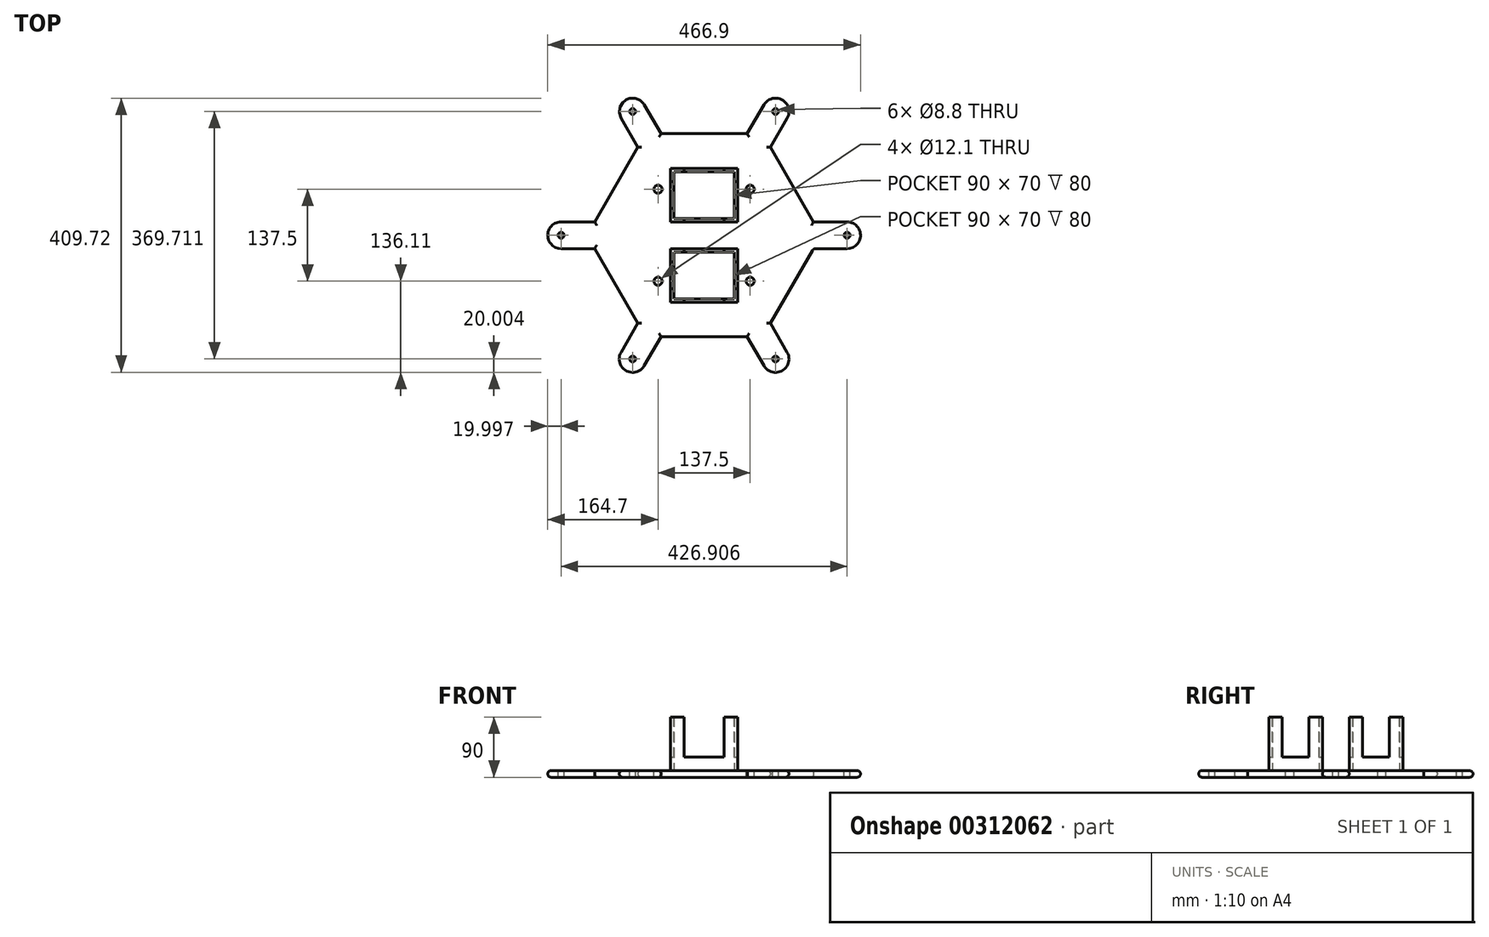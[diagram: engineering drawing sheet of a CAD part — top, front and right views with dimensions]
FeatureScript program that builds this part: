
annotation { "Feature Type Name" : "Feature", "Feature Type Description" : "" }
export const myFeature = defineFeature(function(context is Context, id is Id, definition is map)
    precondition{}
    {
        {
            var Q0;
            Q0=qCreatedBy(makeId("Top.planeOp"),FACE);
            var sketch = newSketch(context, id + "F0", { "sketchPlane" : qUnion([Q0])});
            skCircle(sketch, "E0.cCircle", {"center": v(0, 0) * mm, "radius": 175 * mm, "construction": true});
            skLineSegment(sketch, "E0.0", {"start": v(-87.5, 151.55) * mm, "end": v(87.5, 151.55) * mm});
            skLineSegment(sketch, "E0.1", {"start": v(87.5, 151.55) * mm, "end": v(175, 0) * mm});
            skLineSegment(sketch, "E0.2", {"start": v(175, 0) * mm, "end": v(87.5, -151.55) * mm});
            skLineSegment(sketch, "E0.3", {"start": v(87.5, -151.55) * mm, "end": v(-87.5, -151.55) * mm});
            skLineSegment(sketch, "E0.4", {"start": v(-87.5, -151.55) * mm, "end": v(-175, 0) * mm});
            skLineSegment(sketch, "E0.5", {"start": v(-175, 0) * mm, "end": v(-87.5, 151.55) * mm});
            skLineSegment(sketch, "E1.bottom", {"start": v(-213.45, 20) * mm, "end": v(-163.45, 20) * mm});
            skLineSegment(sketch, "E1.top", {"start": v(-213.45, -20) * mm, "end": v(-163.45, -20) * mm});
            skLineSegment(sketch, "E1.left", {"start": v(-213.45, 20) * mm, "end": v(-213.45, -20) * mm});
            skPoint(sketch, "E2.startSnap0", {"position": v(0, 151.55) * mm});
            skPoint(sketch, "E2.endSnap0", {"position": v(0, -151.55) * mm});
            skLineSegment(sketch, "E3", {"start": v(-175, 0) * mm, "end": v(-213.45, 0) * mm, "construction": true});
            skLineSegment(sketch, "E4.1.0", {"start": v(-124.05, -174.86) * mm, "end": v(-89.4, -194.86) * mm});
            skLineSegment(sketch, "E4.1.1", {"start": v(-124.05, -174.86) * mm, "end": v(-99.05, -131.55) * mm});
            skLineSegment(sketch, "E4.1.2", {"start": v(-89.4, -194.86) * mm, "end": v(-64.4, -151.55) * mm});
            skLineSegment(sketch, "E4.2.0", {"start": v(89.4, -194.86) * mm, "end": v(124.05, -174.86) * mm});
            skLineSegment(sketch, "E4.2.1", {"start": v(89.4, -194.86) * mm, "end": v(64.4, -151.55) * mm});
            skLineSegment(sketch, "E4.2.2", {"start": v(124.05, -174.86) * mm, "end": v(99.05, -131.55) * mm});
            skLineSegment(sketch, "E4.3.0", {"start": v(213.45, -20) * mm, "end": v(213.45, 20) * mm});
            skLineSegment(sketch, "E4.3.1", {"start": v(213.45, -20) * mm, "end": v(163.45, -20) * mm});
            skLineSegment(sketch, "E4.3.2", {"start": v(213.45, 20) * mm, "end": v(163.45, 20) * mm});
            skLineSegment(sketch, "E4.4.0", {"start": v(124.05, 174.86) * mm, "end": v(89.4, 194.86) * mm});
            skLineSegment(sketch, "E4.4.1", {"start": v(124.05, 174.86) * mm, "end": v(99.05, 131.55) * mm});
            skLineSegment(sketch, "E4.4.2", {"start": v(89.4, 194.86) * mm, "end": v(64.4, 151.55) * mm});
            skLineSegment(sketch, "E4.5.0", {"start": v(-89.4, 194.86) * mm, "end": v(-124.05, 174.86) * mm});
            skLineSegment(sketch, "E4.5.1", {"start": v(-89.4, 194.86) * mm, "end": v(-64.4, 151.55) * mm});
            skLineSegment(sketch, "E4.5.2", {"start": v(-124.05, 174.86) * mm, "end": v(-99.05, 131.55) * mm});
            skArc(sketch, "E5", {"start": v(-213.45, 20) * mm, "mid": v(-233.45, 0) * mm, "end": v(-213.45, -20) * mm});
            skArc(sketch, "E6.1.0", {"start": v(-124.05, -174.86) * mm, "mid": v(-116.73, -202.18) * mm, "end": v(-89.4, -194.86) * mm});
            skArc(sketch, "E6.2.0", {"start": v(89.4, -194.86) * mm, "mid": v(116.73, -202.18) * mm, "end": v(124.05, -174.86) * mm});
            skArc(sketch, "E6.3.0", {"start": v(213.45, -20) * mm, "mid": v(233.45, 0) * mm, "end": v(213.45, 20) * mm});
            skArc(sketch, "E6.4.0", {"start": v(124.05, 174.86) * mm, "mid": v(116.73, 202.18) * mm, "end": v(89.4, 194.86) * mm});
            skArc(sketch, "E6.5.0", {"start": v(-89.4, 194.86) * mm, "mid": v(-116.73, 202.18) * mm, "end": v(-124.05, 174.86) * mm});
            skSolve(sketch);
        }
        {
            var Q0;
            Q0=qSketchRegion(id+"F0",true);
            extrude(context, id + "F1", {"entities" : qUnion([Q0]), "depth" : 10 * mm});
        }
        {
            var Q0;
            Q0=makeQuery(id+"F1.opExtrude","CAP_FACE",FACE,{"disambiguationData":[OSD([sQuery(id+"F0.wireOp",EDGE,"E0.0"),sQuery(id+"F0.wireOp",EDGE,"E0.1"),sQuery(id+"F0.wireOp",EDGE,"E0.2"),sQuery(id+"F0.wireOp",EDGE,"E0.3"),sQuery(id+"F0.wireOp",EDGE,"E0.4"),sQuery(id+"F0.wireOp",EDGE,"E0.5"),sQuery(id+"F0.wireOp",EDGE,"E1.bottom"),sQuery(id+"F0.wireOp",EDGE,"E1.top"),sQuery(id+"F0.wireOp",EDGE,"E4.1.1"),sQuery(id+"F0.wireOp",EDGE,"E4.1.2"),sQuery(id+"F0.wireOp",EDGE,"E4.2.1"),sQuery(id+"F0.wireOp",EDGE,"E4.2.2"),sQuery(id+"F0.wireOp",EDGE,"E4.3.1"),sQuery(id+"F0.wireOp",EDGE,"E4.3.2"),sQuery(id+"F0.wireOp",EDGE,"E4.4.1"),sQuery(id+"F0.wireOp",EDGE,"E4.4.2"),sQuery(id+"F0.wireOp",EDGE,"E4.5.1"),sQuery(id+"F0.wireOp",EDGE,"E4.5.2"),sQuery(id+"F0.wireOp",EDGE,"E5"),sQuery(id+"F0.wireOp",EDGE,"E6.1.0"),sQuery(id+"F0.wireOp",EDGE,"E6.2.0"),sQuery(id+"F0.wireOp",EDGE,"E6.3.0"),sQuery(id+"F0.wireOp",EDGE,"E6.4.0"),sQuery(id+"F0.wireOp",EDGE,"E6.5.0")])],"isStart":false});
            var sketch = newSketch(context, id + "F2", { "sketchPlane" : qUnion([Q0])});
            skCircle(sketch, "E7", {"center": v(0, 0) * mm, "radius": 137.5 * mm});
            skCircle(sketch, "E8", {"center": v(0, 0) * mm, "radius": 75 * mm});
            skLineSegment(sketch, "E9", {"start": v(137.5, 0) * mm, "end": v(0, 137.5) * mm});
            skLineSegment(sketch, "E10", {"start": v(0, 137.5) * mm, "end": v(-137.5, 0) * mm});
            skLineSegment(sketch, "E11", {"start": v(-137.5, 0) * mm, "end": v(0, -137.5) * mm});
            skLineSegment(sketch, "E12", {"start": v(0, -137.5) * mm, "end": v(137.5, 0) * mm});
            skLineSegment(sketch, "E13", {"start": v(-75, 0) * mm, "end": v(-106.25, 31.25) * mm});
            skLineSegment(sketch, "E14", {"start": v(0, 75) * mm, "end": v(-31.25, 106.25) * mm});
            skLineSegment(sketch, "E15", {"start": v(0, 75) * mm, "end": v(31.25, 106.25) * mm});
            skLineSegment(sketch, "E16", {"start": v(-75, 0) * mm, "end": v(-106.25, -31.25) * mm});
            skLineSegment(sketch, "E17", {"start": v(0, -75) * mm, "end": v(-31.25, -106.25) * mm});
            skLineSegment(sketch, "E18", {"start": v(0, -75) * mm, "end": v(31.25, -106.25) * mm});
            skLineSegment(sketch, "E19", {"start": v(75, 0) * mm, "end": v(106.25, 31.25) * mm});
            skLineSegment(sketch, "E20", {"start": v(75, 0) * mm, "end": v(106.25, -31.25) * mm});
            skLineSegment(sketch, "E21", {"start": v(0, 75) * mm, "end": v(0, -75) * mm, "construction": true});
            skLineSegment(sketch, "E22", {"start": v(-75, 0) * mm, "end": v(75, 0) * mm, "construction": true});
            skLineSegment(sketch, "E23", {"start": v(-10, 74.33) * mm, "end": v(-10, -74.33) * mm});
            skLineSegment(sketch, "E24", {"start": v(10, 74.33) * mm, "end": v(10, -74.33) * mm});
            skLineSegment(sketch, "E25", {"start": v(-74.33, 10) * mm, "end": v(74.33, 10) * mm});
            skLineSegment(sketch, "E26", {"start": v(74.33, -10) * mm, "end": v(-74.33, -10) * mm});
            skLineSegment(sketch, "E27", {"start": v(-68.75, 68.75) * mm, "end": v(68.75, -68.75) * mm, "construction": true});
            skLineSegment(sketch, "E28", {"start": v(-68.75, -68.75) * mm, "end": v(68.75, 68.75) * mm, "construction": true});
            skPoint(sketch, "E29", {"position": v(-68.75, 68.75) * mm});
            skPoint(sketch, "E30", {"position": v(68.75, 68.75) * mm});
            skPoint(sketch, "E31", {"position": v(-68.75, -68.75) * mm});
            skPoint(sketch, "E32", {"position": v(68.75, -68.75) * mm});
            skSolve(sketch);
        }
        {
            var Q0;
            Q0=makeQuery(id+"F1.opExtrude","CAP_FACE",FACE,{"disambiguationData":[OSD([sQuery(id+"F0.wireOp",EDGE,"E0.0"),sQuery(id+"F0.wireOp",EDGE,"E0.1"),sQuery(id+"F0.wireOp",EDGE,"E0.2"),sQuery(id+"F0.wireOp",EDGE,"E0.3"),sQuery(id+"F0.wireOp",EDGE,"E0.4"),sQuery(id+"F0.wireOp",EDGE,"E0.5"),sQuery(id+"F0.wireOp",EDGE,"E1.bottom"),sQuery(id+"F0.wireOp",EDGE,"E1.top"),sQuery(id+"F0.wireOp",EDGE,"E4.1.1"),sQuery(id+"F0.wireOp",EDGE,"E4.1.2"),sQuery(id+"F0.wireOp",EDGE,"E4.2.1"),sQuery(id+"F0.wireOp",EDGE,"E4.2.2"),sQuery(id+"F0.wireOp",EDGE,"E4.3.1"),sQuery(id+"F0.wireOp",EDGE,"E4.3.2"),sQuery(id+"F0.wireOp",EDGE,"E4.4.1"),sQuery(id+"F0.wireOp",EDGE,"E4.4.2"),sQuery(id+"F0.wireOp",EDGE,"E4.5.1"),sQuery(id+"F0.wireOp",EDGE,"E4.5.2"),sQuery(id+"F0.wireOp",EDGE,"E5"),sQuery(id+"F0.wireOp",EDGE,"E6.1.0"),sQuery(id+"F0.wireOp",EDGE,"E6.2.0"),sQuery(id+"F0.wireOp",EDGE,"E6.3.0"),sQuery(id+"F0.wireOp",EDGE,"E6.4.0"),sQuery(id+"F0.wireOp",EDGE,"E6.5.0")])],"isStart":false});
            var sketch = newSketch(context, id + "F3", { "sketchPlane" : qUnion([Q0])});
            skPoint(sketch, "E33", {"position": v(-213.45, 0) * mm});
            skPoint(sketch, "E34.1.0", {"position": v(-106.73, -184.86) * mm});
            skPoint(sketch, "E34.2.0", {"position": v(106.73, -184.86) * mm});
            skPoint(sketch, "E34.3.0", {"position": v(213.45, 0) * mm});
            skPoint(sketch, "E34.4.0", {"position": v(106.73, 184.86) * mm});
            skPoint(sketch, "E34.5.0", {"position": v(-106.73, 184.86) * mm});
            skPoint(sketch, "E34.center", {"position": v(0, 0) * mm});
            skSolve(sketch);
        }
        {
            var Q0;
            Q0=sQuery(id+"F3.wireOp",VERTEX,"E33");
            var Q1;
            Q1=sQuery(id+"F3.wireOp",VERTEX,"E34.5.0");
            var Q2;
            Q2=sQuery(id+"F3.wireOp",VERTEX,"E34.4.0");
            var Q3;
            Q3=sQuery(id+"F3.wireOp",VERTEX,"E34.3.0");
            var Q4;
            Q4=sQuery(id+"F3.wireOp",VERTEX,"E34.2.0");
            var Q5;
            Q5=sQuery(id+"F3.wireOp",VERTEX,"E34.1.0");
            var Q6;
            Q6=makeQuery(id+"F1.opExtrude","SWEPT_BODY",BODY,{"disambiguationData":[OSD([sQuery(id+"F0.wireOp",EDGE,"E0.0"),sQuery(id+"F0.wireOp",EDGE,"E0.1"),sQuery(id+"F0.wireOp",EDGE,"E0.2"),sQuery(id+"F0.wireOp",EDGE,"E0.3"),sQuery(id+"F0.wireOp",EDGE,"E0.4"),sQuery(id+"F0.wireOp",EDGE,"E0.5"),sQuery(id+"F0.wireOp",EDGE,"E1.bottom"),sQuery(id+"F0.wireOp",EDGE,"E1.top"),sQuery(id+"F0.wireOp",EDGE,"E4.1.1"),sQuery(id+"F0.wireOp",EDGE,"E4.1.2"),sQuery(id+"F0.wireOp",EDGE,"E4.2.1"),sQuery(id+"F0.wireOp",EDGE,"E4.2.2"),sQuery(id+"F0.wireOp",EDGE,"E4.3.1"),sQuery(id+"F0.wireOp",EDGE,"E4.3.2"),sQuery(id+"F0.wireOp",EDGE,"E4.4.1"),sQuery(id+"F0.wireOp",EDGE,"E4.4.2"),sQuery(id+"F0.wireOp",EDGE,"E4.5.1"),sQuery(id+"F0.wireOp",EDGE,"E4.5.2"),sQuery(id+"F0.wireOp",EDGE,"E5"),sQuery(id+"F0.wireOp",EDGE,"E6.1.0"),sQuery(id+"F0.wireOp",EDGE,"E6.2.0"),sQuery(id+"F0.wireOp",EDGE,"E6.3.0"),sQuery(id+"F0.wireOp",EDGE,"E6.4.0"),sQuery(id+"F0.wireOp",EDGE,"E6.5.0")])]});
            hole(context, id + "F4", {"style" : HoleStyle.SIMPLE, "endStyle" : HoleEndStyle.THROUGH, "standardTappedOrClearance" : lookupTablePath({ "standard" : "ISO", "engagement" : "75%", "pitch" : "1.25 mm", "size" : "M10", "type" : "Tapped" }), "standardBlindInLast" : lookupTablePath({ "standard" : "ISO", "engagement" : "75%", "pitch" : "1.25 mm", "size" : "M10", "type" : "Tapped" }), "holeDiameter" : 8.8 * mm, "showTappedDepth" : true, "tappedDepth" : 6 * mm, "tapClearance" : 3, "locations" : qUnion([Q0, Q1, Q2, Q3, Q4, Q5]), "scope" : qUnion([Q6]), "majorDiameter" : 10 * mm});
        }
        {
            var Q0;
            Q0=sQuery(id+"F2.wireOp",VERTEX,"E29");
            var Q1;
            Q1=sQuery(id+"F2.wireOp",VERTEX,"E30");
            var Q2;
            Q2=sQuery(id+"F2.wireOp",VERTEX,"E32");
            var Q3;
            Q3=sQuery(id+"F2.wireOp",VERTEX,"E31");
            var Q4;
            Q4=makeQuery(id+"F1.opExtrude","SWEPT_BODY",BODY,{"disambiguationData":[OSD([sQuery(id+"F0.wireOp",EDGE,"E0.0"),sQuery(id+"F0.wireOp",EDGE,"E0.1"),sQuery(id+"F0.wireOp",EDGE,"E0.2"),sQuery(id+"F0.wireOp",EDGE,"E0.3"),sQuery(id+"F0.wireOp",EDGE,"E0.4"),sQuery(id+"F0.wireOp",EDGE,"E0.5"),sQuery(id+"F0.wireOp",EDGE,"E1.bottom"),sQuery(id+"F0.wireOp",EDGE,"E1.top"),sQuery(id+"F0.wireOp",EDGE,"E4.1.1"),sQuery(id+"F0.wireOp",EDGE,"E4.1.2"),sQuery(id+"F0.wireOp",EDGE,"E4.2.1"),sQuery(id+"F0.wireOp",EDGE,"E4.2.2"),sQuery(id+"F0.wireOp",EDGE,"E4.3.1"),sQuery(id+"F0.wireOp",EDGE,"E4.3.2"),sQuery(id+"F0.wireOp",EDGE,"E4.4.1"),sQuery(id+"F0.wireOp",EDGE,"E4.4.2"),sQuery(id+"F0.wireOp",EDGE,"E4.5.1"),sQuery(id+"F0.wireOp",EDGE,"E4.5.2"),sQuery(id+"F0.wireOp",EDGE,"E5"),sQuery(id+"F0.wireOp",EDGE,"E6.1.0"),sQuery(id+"F0.wireOp",EDGE,"E6.2.0"),sQuery(id+"F0.wireOp",EDGE,"E6.3.0"),sQuery(id+"F0.wireOp",EDGE,"E6.4.0"),sQuery(id+"F0.wireOp",EDGE,"E6.5.0")])]});
            hole(context, id + "F5", {"style" : HoleStyle.SIMPLE, "endStyle" : HoleEndStyle.THROUGH, "standardTappedOrClearance" : lookupTablePath({ "standard" : "ISO", "engagement" : "75%", "pitch" : "2 mm", "size" : "M14", "type" : "Tapped" }), "standardBlindInLast" : lookupTablePath({ "standard" : "ISO", "engagement" : "75%", "pitch" : "2 mm", "size" : "M14", "type" : "Tapped" }), "holeDiameter" : 12.1 * mm, "showTappedDepth" : true, "tappedDepth" : 6 * mm, "tapClearance" : 3, "locations" : qUnion([Q0, Q1, Q2, Q3]), "scope" : qUnion([Q4]), "majorDiameter" : 14 * mm});
        }
        {
            var Q0;
            Q0=makeQuery(id+"F3.imprint","IMPRINT",FACE,{"disambiguationData":[TD([[makeQuery(id+"F3.imprint","IMPRINT",EDGE,{"derivedFrom":makeQuery(id+"F1.opExtrude","CAP_EDGE",EDGE,{"disambiguationData":[OSD([sQuery(id+"F0.wireOp",EDGE,"E0.0")])],"isStart":false})}),-1.0]])]});
            var sketch = newSketch(context, id + "F6", { "sketchPlane" : qUnion([Q0])});
            skLineSegment(sketch, "E35.bottom", {"start": v(-60, 60) * mm, "end": v(60, 60) * mm, "construction": true});
            skLineSegment(sketch, "E35.top", {"start": v(-60, -60) * mm, "end": v(60, -60) * mm, "construction": true});
            skLineSegment(sketch, "E35.left", {"start": v(-60, 60) * mm, "end": v(-60, -60) * mm, "construction": true});
            skLineSegment(sketch, "E35.right", {"start": v(60, 60) * mm, "end": v(60, -60) * mm, "construction": true});
            skPoint(sketch, "E35.middle", {"position": v(0, 0) * mm});
            skLineSegment(sketch, "E36", {"start": v(0, -60) * mm, "end": v(0, 60) * mm, "construction": true});
            skLineSegment(sketch, "E37", {"start": v(-60, 0) * mm, "end": v(60, 0) * mm, "construction": true});
            skPoint(sketch, "E38", {"position": v(0, 60) * mm});
            skPoint(sketch, "E39", {"position": v(0, -60) * mm});
            skPoint(sketch, "E40", {"position": v(60, 0) * mm});
            skPoint(sketch, "E41", {"position": v(-60, 0) * mm});
            skLineSegment(sketch, "E42.bottom", {"start": v(-50, 100) * mm, "end": v(50, 100) * mm});
            skLineSegment(sketch, "E42.top", {"start": v(-50, 20) * mm, "end": v(50, 20) * mm});
            skLineSegment(sketch, "E42.left", {"start": v(-50, 100) * mm, "end": v(-50, 20) * mm});
            skLineSegment(sketch, "E42.right", {"start": v(50, 100) * mm, "end": v(50, 20) * mm});
            skLineSegment(sketch, "E43.bottom", {"start": v(-50, -20) * mm, "end": v(50, -20) * mm});
            skLineSegment(sketch, "E43.top", {"start": v(-50, -100) * mm, "end": v(50, -100) * mm});
            skLineSegment(sketch, "E43.left", {"start": v(-50, -20) * mm, "end": v(-50, -100) * mm});
            skLineSegment(sketch, "E43.right", {"start": v(50, -20) * mm, "end": v(50, -100) * mm});
            skLineSegment(sketch, "E44.bottom", {"start": v(-45, 95) * mm, "end": v(45, 95) * mm});
            skLineSegment(sketch, "E44.top", {"start": v(-45, 25) * mm, "end": v(45, 25) * mm});
            skLineSegment(sketch, "E44.left", {"start": v(-45, 95) * mm, "end": v(-45, 25) * mm});
            skLineSegment(sketch, "E44.right", {"start": v(45, 95) * mm, "end": v(45, 25) * mm});
            skLineSegment(sketch, "E45.bottom", {"start": v(-45, -25) * mm, "end": v(45, -25) * mm});
            skLineSegment(sketch, "E45.top", {"start": v(-45, -95) * mm, "end": v(45, -95) * mm});
            skLineSegment(sketch, "E45.left", {"start": v(-45, -25) * mm, "end": v(-45, -95) * mm});
            skLineSegment(sketch, "E45.right", {"start": v(45, -25) * mm, "end": v(45, -95) * mm});
            skSolve(sketch);
        }
        {
            var Q0;
            Q0 = qSketchRegion(id + "F6", true);
            extrude(context, id + "F7", {"entities" : qUnion([Q0]), "operationType" : NewBodyOperationType.ADD, "depth" : 80 * mm});
        }
        {
            var Q0;
            Q0=makeQuery(id+"F7.opExtrude","SWEPT_FACE",FACE,{"disambiguationData":[OSD([sQuery(id+"F6.wireOp",EDGE,"E42.bottom")])]});
            var sketch = newSketch(context, id + "F8", { "sketchPlane" : qUnion([Q0])});
            skLineSegment(sketch, "E46.bottom", {"start": v(30, 30) * mm, "end": v(-30, 30) * mm});
            skLineSegment(sketch, "E46.top", {"start": v(30, 150) * mm, "end": v(-30, 150) * mm});
            skLineSegment(sketch, "E46.left", {"start": v(30, 30) * mm, "end": v(30, 150) * mm});
            skLineSegment(sketch, "E46.right", {"start": v(-30, 30) * mm, "end": v(-30, 150) * mm});
            skPoint(sketch, "E46.middle", {"position": v(0, 90) * mm});
            skSolve(sketch);
        }
        {
            var Q0;
            Q0 = qSketchRegion(id + "F8", true);
            extrude(context, id + "F9", {"entities" : qUnion([Q0]), "operationType" : NewBodyOperationType.REMOVE, "endBound" : BoundingType.THROUGH_ALL, "oppositeDirection" : true, "depth" : 25 * mm});
        }
        {
            var Q0;
            Q0=makeQuery(id+"F7.opExtrude","SWEPT_FACE",FACE,{"disambiguationData":[OSD([sQuery(id+"F6.wireOp",EDGE,"E42.right")])]});
            var sketch = newSketch(context, id + "F10", { "sketchPlane" : qUnion([Q0])});
            skLineSegment(sketch, "E47.bottom", {"start": v(80, 30) * mm, "end": v(40, 30) * mm});
            skLineSegment(sketch, "E47.top", {"start": v(80, 150) * mm, "end": v(40, 150) * mm});
            skLineSegment(sketch, "E47.left", {"start": v(80, 30) * mm, "end": v(80, 150) * mm});
            skLineSegment(sketch, "E47.right", {"start": v(40, 30) * mm, "end": v(40, 150) * mm});
            skPoint(sketch, "E47.middle", {"position": v(60, 90) * mm});
            skSolve(sketch);
        }
        {
            var Q0;
            Q0 = qSketchRegion(id + "F10", true);
            extrude(context, id + "F11", {"entities" : qUnion([Q0]), "operationType" : NewBodyOperationType.REMOVE, "endBound" : BoundingType.THROUGH_ALL, "oppositeDirection" : true, "depth" : 25 * mm});
        }
        {
            var Q0;
            Q0=makeQuery(id+"F7.opExtrude","SWEPT_FACE",FACE,{"disambiguationData":[OSD([sQuery(id+"F6.wireOp",EDGE,"E43.right")])]});
            var sketch = newSketch(context, id + "F12", { "sketchPlane" : qUnion([Q0])});
            skLineSegment(sketch, "E48.bottom", {"start": v(-40, 30) * mm, "end": v(-80, 30) * mm});
            skLineSegment(sketch, "E48.top", {"start": v(-40, 150) * mm, "end": v(-80, 150) * mm});
            skLineSegment(sketch, "E48.left", {"start": v(-40, 30) * mm, "end": v(-40, 150) * mm});
            skLineSegment(sketch, "E48.right", {"start": v(-80, 30) * mm, "end": v(-80, 150) * mm});
            skPoint(sketch, "E48.middle", {"position": v(-60, 90) * mm});
            skSolve(sketch);
        }
        {
            var Q0;
            Q0 = qSketchRegion(id + "F12", true);
            extrude(context, id + "F13", {"entities" : qUnion([Q0]), "operationType" : NewBodyOperationType.REMOVE, "endBound" : BoundingType.THROUGH_ALL, "oppositeDirection" : true, "depth" : 25 * mm});
        }
        {
            var Q0;
            Q0=makeQuery(id+"F1.opExtrude","CAP_EDGE",EDGE,{"disambiguationData":[OSD([sQuery(id+"F0.wireOp",EDGE,"E0.2")])],"isStart":false});
            var Q1;
            Q1=makeQuery(id+"F1.opExtrude","CAP_EDGE",EDGE,{"disambiguationData":[OSD([sQuery(id+"F0.wireOp",EDGE,"E0.2")])],"isStart":true});
            var Q2;
            Q2=makeQuery(id+"F1.opExtrude","SWEPT_FACE",FACE,{"disambiguationData":[OSD([sQuery(id+"F0.wireOp",EDGE,"E4.3.1")])]});
            var Q3;
            Q3=makeQuery(id+"F1.opExtrude","CAP_EDGE",EDGE,{"disambiguationData":[OSD([sQuery(id+"F0.wireOp",EDGE,"E6.2.0")])],"isStart":false});
            var Q4;
            Q4=makeQuery(id+"F1.opExtrude","CAP_EDGE",EDGE,{"disambiguationData":[OSD([sQuery(id+"F0.wireOp",EDGE,"E0.3")])],"isStart":false});
            var Q5;
            Q5=makeQuery(id+"F1.opExtrude","CAP_EDGE",EDGE,{"disambiguationData":[OSD([sQuery(id+"F0.wireOp",EDGE,"E0.3")])],"isStart":true});
            var Q6;
            Q6=makeQuery(id+"F1.opExtrude","CAP_EDGE",EDGE,{"disambiguationData":[OSD([sQuery(id+"F0.wireOp",EDGE,"E6.3.0")])],"isStart":true});
            var Q7;
            Q7=makeQuery(id+"F1.opExtrude","CAP_EDGE",EDGE,{"disambiguationData":[OSD([sQuery(id+"F0.wireOp",EDGE,"E0.1")])],"isStart":true});
            var Q8;
            Q8=makeQuery(id+"F1.opExtrude","CAP_EDGE",EDGE,{"disambiguationData":[OSD([sQuery(id+"F0.wireOp",EDGE,"E4.4.1")])],"isStart":true});
            var Q9;
            Q9=makeQuery(id+"F1.opExtrude","CAP_EDGE",EDGE,{"disambiguationData":[OSD([sQuery(id+"F0.wireOp",EDGE,"E0.1")])],"isStart":false});
            var Q10;
            Q10=makeQuery(id+"F1.opExtrude","CAP_EDGE",EDGE,{"disambiguationData":[OSD([sQuery(id+"F0.wireOp",EDGE,"E6.4.0")])],"isStart":true});
            var Q11;
            Q11=makeQuery(id+"F1.opExtrude","CAP_EDGE",EDGE,{"disambiguationData":[OSD([sQuery(id+"F0.wireOp",EDGE,"E4.4.1")])],"isStart":false});
            var Q12;
            Q12=makeQuery(id+"F1.opExtrude","CAP_EDGE",EDGE,{"disambiguationData":[OSD([sQuery(id+"F0.wireOp",EDGE,"E6.4.0")])],"isStart":false});
            var Q13;
            Q13=makeQuery(id+"F1.opExtrude","CAP_EDGE",EDGE,{"disambiguationData":[OSD([sQuery(id+"F0.wireOp",EDGE,"E0.0")])],"isStart":false});
            var Q14;
            Q14=makeQuery(id+"F1.opExtrude","CAP_EDGE",EDGE,{"disambiguationData":[OSD([sQuery(id+"F0.wireOp",EDGE,"E0.0")])],"isStart":true});
            var Q15;
            Q15=makeQuery(id+"F1.opExtrude","CAP_EDGE",EDGE,{"disambiguationData":[OSD([sQuery(id+"F0.wireOp",EDGE,"E4.5.1")])],"isStart":false});
            var Q16;
            Q16=makeQuery(id+"F1.opExtrude","CAP_EDGE",EDGE,{"disambiguationData":[OSD([sQuery(id+"F0.wireOp",EDGE,"E4.5.1")])],"isStart":true});
            var Q17;
            Q17=makeQuery(id+"F1.opExtrude","CAP_EDGE",EDGE,{"disambiguationData":[OSD([sQuery(id+"F0.wireOp",EDGE,"E6.5.0")])],"isStart":false});
            var Q18;
            Q18=makeQuery(id+"F1.opExtrude","CAP_EDGE",EDGE,{"disambiguationData":[OSD([sQuery(id+"F0.wireOp",EDGE,"E4.5.2")])],"isStart":true});
            var Q19;
            Q19=makeQuery(id+"F1.opExtrude","CAP_EDGE",EDGE,{"disambiguationData":[OSD([sQuery(id+"F0.wireOp",EDGE,"E6.5.0")])],"isStart":true});
            var Q20;
            Q20=makeQuery(id+"F1.opExtrude","CAP_EDGE",EDGE,{"disambiguationData":[OSD([sQuery(id+"F0.wireOp",EDGE,"E0.5")])],"isStart":true});
            var Q21;
            Q21=makeQuery(id+"F1.opExtrude","CAP_EDGE",EDGE,{"disambiguationData":[OSD([sQuery(id+"F0.wireOp",EDGE,"E1.bottom")])],"isStart":true});
            var Q22;
            Q22=makeQuery(id+"F1.opExtrude","CAP_EDGE",EDGE,{"disambiguationData":[OSD([sQuery(id+"F0.wireOp",EDGE,"E1.top")])],"isStart":true});
            var Q23;
            Q23=makeQuery(id+"F1.opExtrude","CAP_EDGE",EDGE,{"disambiguationData":[OSD([sQuery(id+"F0.wireOp",EDGE,"E0.4")])],"isStart":true});
            var Q24;
            Q24=makeQuery(id+"F1.opExtrude","CAP_EDGE",EDGE,{"disambiguationData":[OSD([sQuery(id+"F0.wireOp",EDGE,"E4.1.1")])],"isStart":true});
            var Q25;
            Q25=makeQuery(id+"F1.opExtrude","CAP_EDGE",EDGE,{"disambiguationData":[OSD([sQuery(id+"F0.wireOp",EDGE,"E6.1.0")])],"isStart":true});
            var Q26;
            Q26=makeQuery(id+"F1.opExtrude","CAP_EDGE",EDGE,{"disambiguationData":[OSD([sQuery(id+"F0.wireOp",EDGE,"E4.1.2")])],"isStart":true});
            var Q27;
            Q27=makeQuery(id+"F1.opExtrude","CAP_EDGE",EDGE,{"disambiguationData":[OSD([sQuery(id+"F0.wireOp",EDGE,"E4.2.1")])],"isStart":true});
            var Q28;
            Q28=makeQuery(id+"F1.opExtrude","CAP_EDGE",EDGE,{"disambiguationData":[OSD([sQuery(id+"F0.wireOp",EDGE,"E6.2.0")])],"isStart":true});
            var Q29;
            Q29=makeQuery(id+"F1.opExtrude","CAP_EDGE",EDGE,{"disambiguationData":[OSD([sQuery(id+"F0.wireOp",EDGE,"E4.4.2")])],"isStart":true});
            var Q30;
            Q30=makeQuery(id+"F1.opExtrude","CAP_EDGE",EDGE,{"disambiguationData":[OSD([sQuery(id+"F0.wireOp",EDGE,"E4.3.2")])],"isStart":true});
            var Q31;
            Q31=makeQuery(id+"F1.opExtrude","CAP_EDGE",EDGE,{"disambiguationData":[OSD([sQuery(id+"F0.wireOp",EDGE,"E4.2.2")])],"isStart":true});
            var Q32;
            Q32=makeQuery(id+"F1.opExtrude","CAP_EDGE",EDGE,{"disambiguationData":[OSD([sQuery(id+"F0.wireOp",EDGE,"E5")])],"isStart":true});
            var Q33;
            Q33=makeQuery(id+"F1.opExtrude","CAP_EDGE",EDGE,{"disambiguationData":[OSD([sQuery(id+"F0.wireOp",EDGE,"E4.1.2")])],"isStart":false});
            var Q34;
            Q34=makeQuery(id+"F1.opExtrude","CAP_EDGE",EDGE,{"disambiguationData":[OSD([sQuery(id+"F0.wireOp",EDGE,"E1.top")])],"isStart":false});
            var Q35;
            Q35=makeQuery(id+"F1.opExtrude","CAP_EDGE",EDGE,{"disambiguationData":[OSD([sQuery(id+"F0.wireOp",EDGE,"E5")])],"isStart":false});
            var Q36;
            Q36=makeQuery(id+"F1.opExtrude","CAP_EDGE",EDGE,{"disambiguationData":[OSD([sQuery(id+"F0.wireOp",EDGE,"E1.bottom")])],"isStart":false});
            var Q37;
            Q37=makeQuery(id+"F1.opExtrude","CAP_EDGE",EDGE,{"disambiguationData":[OSD([sQuery(id+"F0.wireOp",EDGE,"E0.5")])],"isStart":false});
            var Q38;
            Q38=makeQuery(id+"F1.opExtrude","CAP_EDGE",EDGE,{"disambiguationData":[OSD([sQuery(id+"F0.wireOp",EDGE,"E4.4.2")])],"isStart":false});
            var Q39;
            Q39=makeQuery(id+"F1.opExtrude","CAP_EDGE",EDGE,{"disambiguationData":[OSD([sQuery(id+"F0.wireOp",EDGE,"E4.3.2")])],"isStart":false});
            var Q40;
            Q40=makeQuery(id+"F1.opExtrude","CAP_EDGE",EDGE,{"disambiguationData":[OSD([sQuery(id+"F0.wireOp",EDGE,"E6.3.0")])],"isStart":false});
            var Q41;
            Q41=makeQuery(id+"F1.opExtrude","CAP_EDGE",EDGE,{"disambiguationData":[OSD([sQuery(id+"F0.wireOp",EDGE,"E4.2.2")])],"isStart":false});
            var Q42;
            Q42=makeQuery(id+"F1.opExtrude","CAP_EDGE",EDGE,{"disambiguationData":[OSD([sQuery(id+"F0.wireOp",EDGE,"E4.2.1")])],"isStart":false});
            var Q43;
            Q43=makeQuery(id+"F1.opExtrude","CAP_EDGE",EDGE,{"disambiguationData":[OSD([sQuery(id+"F0.wireOp",EDGE,"E6.1.0")])],"isStart":false});
            var Q44;
            Q44=makeQuery(id+"F1.opExtrude","CAP_EDGE",EDGE,{"disambiguationData":[OSD([sQuery(id+"F0.wireOp",EDGE,"E4.1.1")])],"isStart":false});
            var Q45;
            Q45=makeQuery(id+"F1.opExtrude","CAP_EDGE",EDGE,{"disambiguationData":[OSD([sQuery(id+"F0.wireOp",EDGE,"E0.4")])],"isStart":false});
            var Q46;
            Q46=makeQuery(id+"F1.opExtrude","CAP_EDGE",EDGE,{"disambiguationData":[OSD([sQuery(id+"F0.wireOp",EDGE,"E4.5.2")])],"isStart":false});
            fillet(context, id + "F14", {"entities" : qUnion([Q0, Q1, Q2, Q3, Q4, Q5, Q6, Q7, Q8, Q9, Q10, Q11, Q12, Q13, Q14, Q15, Q16, Q17, Q18, Q19, Q20, Q21, Q22, Q23, Q24, Q25, Q26, Q27, Q28, Q29, Q30, Q31, Q32, Q33, Q34, Q35, Q36, Q37, Q38, Q39, Q40, Q41, Q42, Q43, Q44, Q45, Q46]), "radius" : 5 * mm, "tangentPropagation" : true, "allowEdgeOverflow" : false});
        }
    });
